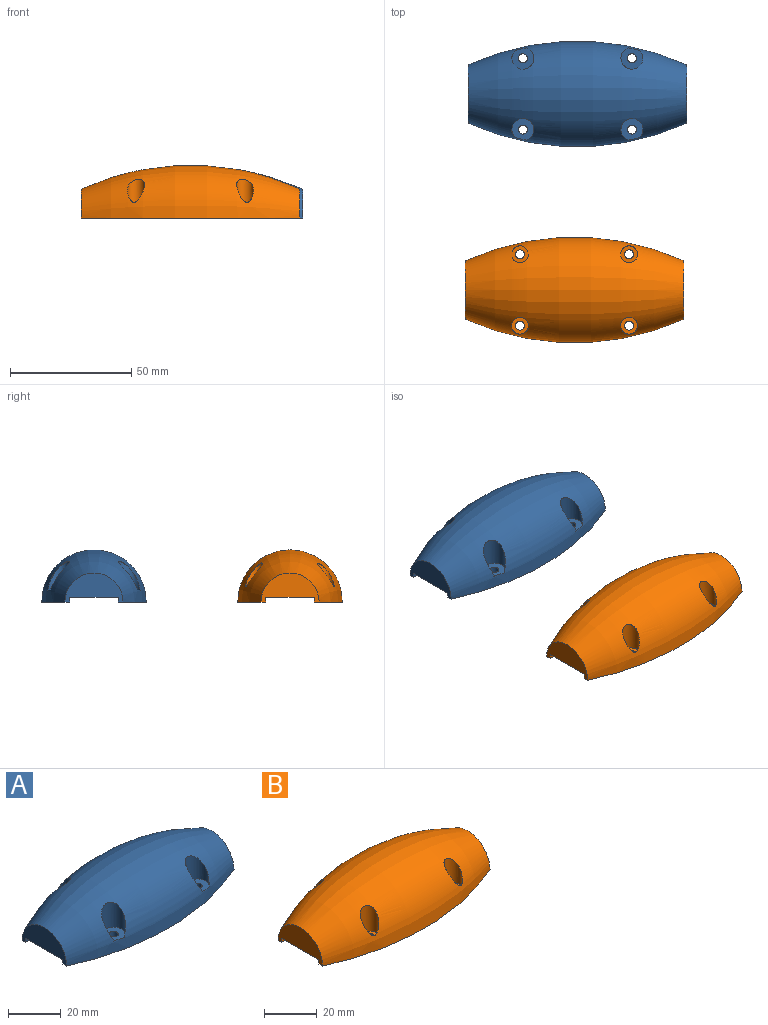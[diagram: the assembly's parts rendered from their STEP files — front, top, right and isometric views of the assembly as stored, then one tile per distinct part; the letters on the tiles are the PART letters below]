
ASSEMBLY  parts=2 mates=1
PART A: 20 faces, bbox 90x43.6x21.8 mm
  f0: cylinder r=1.85mm len=5mm, axis (0,0,-1), area 58.1mm2, adj f3,f17
  f1: cylinder r=1.85mm len=5mm, axis (0,0,-1), area 58.1mm2, adj f3,f19
  f2: revolved ~90x43.56mm, area 4956.3mm2, adj f3,f4,f5,f6,f12,f13,f14,f15
  f3: plane 90x11.78mm, normal (0,0,-1), area 750.9mm2, adj f0,f1,f2,f5,f6,f8
  f4: plane 90x11.78mm, normal (0,0,-1), area 750.9mm2, adj f2,f5,f6,f9,f10,f11
  f5: plane 24x12mm, normal (-1,0,0), area 186.2mm2, adj f2,f3,f4,f7,f8,f9
  f6: plane 24x12mm, normal (1,0,0), area 186.2mm2, adj f2,f3,f4,f7,f8,f9
  f7: plane 90x20mm, normal (0,0,-1), area 1800mm2, adj f5,f6,f8,f9
  f8: plane 90x2mm, normal (0,1,0), area 180mm2, adj f3,f5,f6,f7
  f9: plane 90x2mm, normal (0,-1,0), area 180mm2, adj f4,f5,f6,f7
  f10: cylinder r=1.85mm len=5mm, axis (0,0,-1), area 58.1mm2, adj f4,f15
  f11: cylinder r=1.85mm len=5mm, axis (0,0,-1), area 58.1mm2, adj f4,f13
  f12: cylinder r=4.55mm len=11.76mm, axis (0,0,-1), area 186.1mm2, adj f2,f13
  f13: plane 9.12x8.92mm, normal (0,0,1), area 52.5mm2, adj f2,f11,f12
  f14: cylinder r=4.55mm len=11.76mm, axis (0,0,-1), area 186.1mm2, adj f2,f15
  f15: plane 9.12x8.91mm, normal (0,0,1), area 52.5mm2, adj f2,f10,f14
  f16: cylinder r=4.55mm len=11.76mm, axis (0,0,-1), area 186.1mm2, adj f2,f17
  f17: plane 9.12x8.91mm, normal (0,0,1), area 52.5mm2, adj f0,f2,f16
  f18: cylinder r=4.55mm len=11.76mm, axis (0,0,-1), area 186.1mm2, adj f2,f19
  f19: plane 9.12x8.92mm, normal (0,0,1), area 52.5mm2, adj f1,f2,f18
PART B: 20 faces, bbox 90x43.6x21.8 mm
  f0: cylinder r=1.85mm len=4mm, axis (0,0,-1), area 46.5mm2, adj f4,f13
  f1: cylinder r=1.85mm len=4mm, axis (0,0,-1), area 46.5mm2, adj f5,f15
  f2: cylinder r=1.85mm len=4mm, axis (0,0,-1), area 46.5mm2, adj f4,f19
  f3: revolved ~90x43.56mm, area 5136.9mm2, adj f4,f5,f6,f7,f12,f14,f16,f18
  f4: plane 90x11.78mm, normal (0,0,-1), area 750.9mm2, adj f0,f2,f3,f6,f7,f9
  f5: plane 90x11.78mm, normal (0,0,-1), area 750.9mm2, adj f1,f3,f6,f7,f10,f11
  f6: plane 24x12mm, normal (-1,0,0), area 186.2mm2, adj f3,f4,f5,f8,f9,f10
  f7: plane 24x12mm, normal (1,0,0), area 186.2mm2, adj f3,f4,f5,f8,f9,f10
  f8: plane 90x20mm, normal (0,0,-1), area 1800mm2, adj f6,f7,f9,f10
  f9: plane 90x2mm, normal (0,1,0), area 180mm2, adj f4,f6,f7,f8
  f10: plane 90x2mm, normal (0,-1,0), area 180mm2, adj f5,f6,f7,f8
  f11: cylinder r=1.85mm len=4mm, axis (0,0,-1), area 46.5mm2, adj f5,f17
  f12: cylinder r=3.5mm len=12.01mm, axis (0,0,-1), area 174.9mm2, adj f3,f13
  f13: plane 7x7mm, normal (0,0,1), area 27.7mm2, adj f0,f12
  f14: cylinder r=3.5mm len=12.01mm, axis (0,0,-1), area 175mm2, adj f3,f15
  f15: plane 7x7mm, normal (0,0,1), area 27.7mm2, adj f1,f14
  f16: cylinder r=3.5mm len=12.01mm, axis (0,0,-1), area 174.9mm2, adj f3,f17
  f17: plane 7x7mm, normal (0,0,1), area 27.7mm2, adj f11,f16
  f18: cylinder r=3.5mm len=12.01mm, axis (0,0,-1), area 174.9mm2, adj f3,f19
  f19: plane 7x7mm, normal (0,0,1), area 27.7mm2, adj f2,f18
PLACE A t=(-86.98,-3.75,23.36)mm
PLACE B t=(75.14,-84.62,23.36)mm
MATE planar B.f8 <-> A.f7  axis (0,0,-1) through (-36.63,-84.62,25.36)mm
